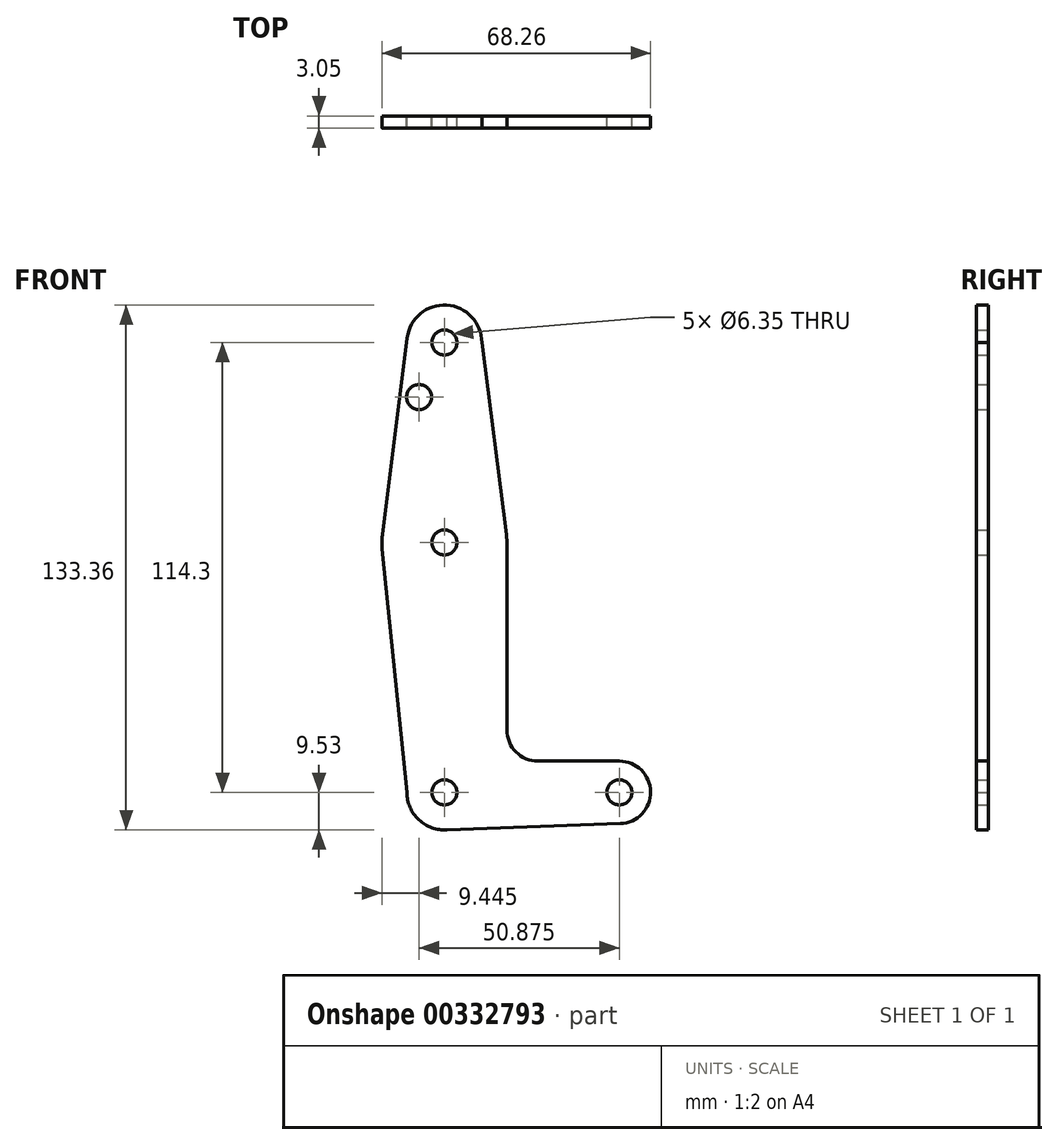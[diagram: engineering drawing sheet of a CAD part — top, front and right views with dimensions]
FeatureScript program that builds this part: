
annotation { "Feature Type Name" : "Feature", "Feature Type Description" : "" }
export const myFeature = defineFeature(function(context is Context, id is Id, definition is map)
    precondition{}
    {
        {
            var Q0;
            Q0=qCreatedBy(makeId("Front.planeOp"),FACE);
            var sketch = newSketch(context, id + "F0", { "sketchPlane" : qUnion([Q0])});
            skLineSegment(sketch, "E0", {"start": v(0, 0) * mm, "end": v(0, 114.3) * mm});
            skCircle(sketch, "E1", {"center": v(0, 114.3) * mm, "radius": 9.53 * mm});
            skLineSegment(sketch, "E2", {"start": v(0, 0) * mm, "end": v(44.45, 0) * mm});
            skCircle(sketch, "E3", {"center": v(0, 0) * mm, "radius": 9.53 * mm});
            skCircle(sketch, "E4", {"center": v(44.45, 0) * mm, "radius": 7.94 * mm});
            skCircle(sketch, "E5", {"center": v(0, 63.5) * mm, "radius": 15.88 * mm});
            skLineSegment(sketch, "E6", {"start": v(-9.45, 115.5) * mm, "end": v(-15.75, 65.48) * mm});
            skLineSegment(sketch, "E7", {"start": v(9.53, 114.3) * mm, "end": v(15.75, 65.5) * mm});
            skLineSegment(sketch, "E8", {"start": v(0, -9.52) * mm, "end": v(44.73, -7.93) * mm});
            skCircle(sketch, "E9", {"center": v(0, 114.3) * mm, "radius": 3.18 * mm});
            skCircle(sketch, "E10", {"center": v(0, 63.5) * mm, "radius": 3.18 * mm});
            skCircle(sketch, "E11", {"center": v(0, 0) * mm, "radius": 3.18 * mm});
            skCircle(sketch, "E12", {"center": v(44.45, 0) * mm, "radius": 3.18 * mm});
            skLineSegment(sketch, "E13", {"start": v(15.87, 63.5) * mm, "end": v(15.88, 15.89) * mm});
            skLineSegment(sketch, "E14", {"start": v(23.83, 7.94) * mm, "end": v(44.45, 7.94) * mm});
            skArc(sketch, "E15.filletArc", {"start": v(15.88, 15.89) * mm, "mid": v(18.2, 10.27) * mm, "end": v(23.83, 7.94) * mm});
            skLineSegment(sketch, "E16", {"start": v(-9.53, 0) * mm, "end": v(-15.8, 61.9) * mm});
            skCircle(sketch, "E17", {"center": v(-6.43, 100.44) * mm, "radius": 3.18 * mm});
            skSolve(sketch);
        }
        {
            var Q0;
            Q0 = qSketchRegion(id + "F0", true);
            var Q1;
            {var subQ0=sQuery(id+"F0.wireOp",EDGE,"E11");var subQ1=sQuery(id+"F0.wireOp",EDGE,"E0");var subQ2=makeQuery(id+"F0.imprint","INTERSECT",VERTEX,{"derivedFrom":[subQ1,subQ0]});Q1=makeQuery(id+"F0.imprint","IMPRINT",FACE,{"disambiguationData":[TD([[makeQuery(id+"F0.imprint","IMPRINT",EDGE,{"disambiguationData":[TD([[subQ2,-1.0]])],"derivedFrom":subQ1}),-1.0]])]});}
            extrude(context, id + "F1", {"entities" : qUnion([Q0, Q1]), "depth" : 3.05 * mm});
        }
    });
